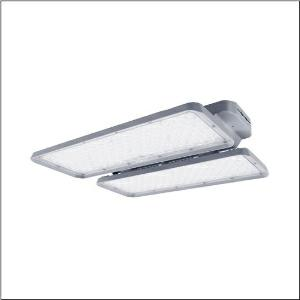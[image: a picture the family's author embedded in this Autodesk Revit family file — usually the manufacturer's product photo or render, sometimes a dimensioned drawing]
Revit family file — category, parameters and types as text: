
# Revit family: highbay_21-l_51hk42db4qca
name_source: partatom
category: Lighting Fixtures
units: mm (PartAtom-declared; Revit-internal decimal feet)

## family parameters
Cut with Voids When Loaded = No
Host = Face
Light Source = No
Part Type = Normal
Room Calculation Point = No
Round Connector Dimension = Use Diameter
Shared = No

## types (1)
- Highbay 21-L (1 x LED, 36000 lm, 200 W, 4000K)
    Apparent Load = 200 VA
    CIE Flux Codes = 75 96 99 100 100
    Color Rendering = 80
    Color Temperature = 4000K
    Default Elevation = 1800 mm
    Description = Highbay 21-L, LED high bay luminaire, primary light control with lens, of PC, light emission: direct distribution, primary light characteristic: symmetric, installation type: suspended mounting, surface-mounted, LED, rated luminous flux: 36.000lm, luminous efficacy: 180lm/W, light colour: 840, colour temperature: 4000K, with terminal, 5-pole, max. 2.5mm², mains connection: 220..240V, AC, 50Hz, rated input power: 200W, housing, of diecast aluminium, coated, grey, length: 471mm, width: 390mm, height: 87mm, protection rating (complete): IP66, insulation class (complete): insulation class I (protective earthing), certification: CE, ENEC, UKCA, protection symbol: D, impact resistance: IK08, permissible operating ambient temperature: -30..+60°C, corresponds to IFS (International Featured Standards) requirements for safety and quality in the food industry, LABS conformity tested according to VDMA 24364:2018-05, packaging unit: 1 piece
    Height = 89 mm
    Lamp = 1 x LED
    Lamp Light Flux = 36000 lm
    Lamp Power = 200 W
    Lamp count = 1
    Length = 471 mm
    Luminous efficacy = 180 lm/W
    Manufacturer = Siteco
    ModVariant = No
    Model = 51HK42DB4QCA
    Mounting Place = Ceiling
    Mounting Type = Pendant
    Number of Poles = 1
    OnlyDefault = Yes
    Power Factor = 1
    Product Name = Highbay 21-L
    Product group = LED high bay luminaire
    ProductGroupID = 903
    Protection Class = Protection class I
    Protection Degree = IP 66
    RLX_Detail_Level = 1
    RLX_Emergency_Light_Flux = 0 lm
    RLX_Emergency_Type = 0
    RLX_Emergency_Type_DB = No
    RlxData = <blob elided: 25957 chars, md5=8f494594>
    Socket = socket
    Standby Power = 0 W
    System Light Flux = 36000 lm
    System Power = 200 W
    Type Comments = Product without accessories
    Type Image = l_1276530.jpg
    URL = http://relux.com
    VarID = ---
    Voltage = 0 V
    Weight = 0.00 kg
    Width = 390 mm

## geometry (parser evidence)
native form markers: Blend x4, Sweep x11
no freeform markers — native parametric forms only
